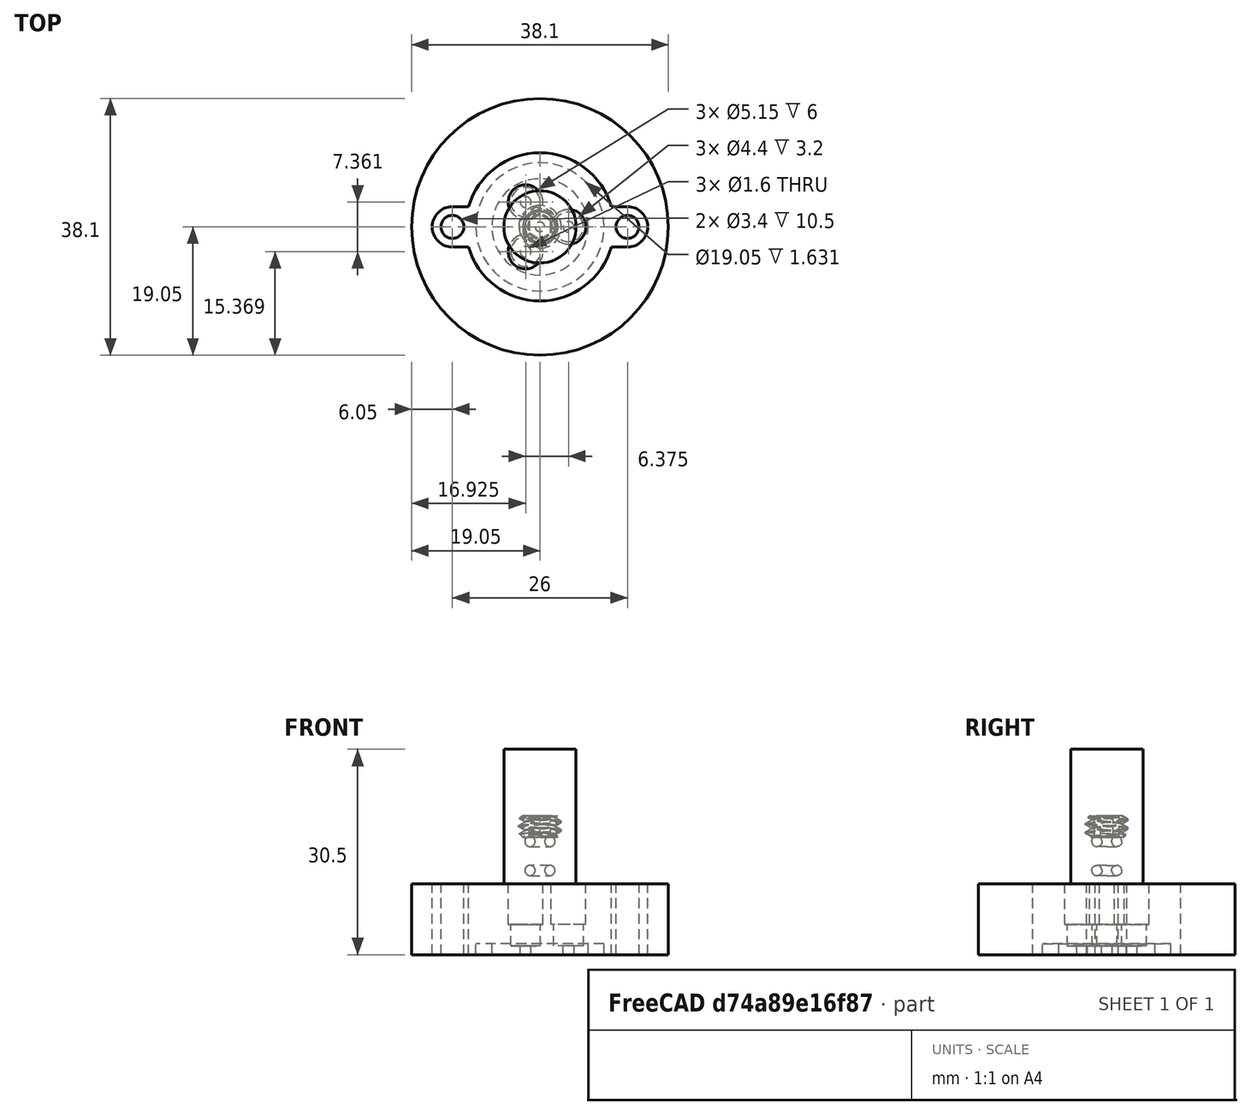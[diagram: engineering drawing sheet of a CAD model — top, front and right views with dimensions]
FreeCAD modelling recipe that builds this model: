
FCSTD DOCUMENT  (FreeCAD 0.18RUnknown)
Label: new_wire_fts_bottom
License: All rights reserved
LicenseURL: http://en.wikipedia.org/wiki/All_rights_reserved
objects: Part::Cylinder×21, Part::MultiFuse×6, Part::Cut×4, Part::Box×4, Part::FeaturePython×4, Part::Feature×3, Path::FeaturePython×3, App::FeaturePython×1, App::DocumentObjectGroup×1, Path::FeatureCompoundPython×1
note: 43 computed .brp shape members not serialized (recipe doc carries the construction recipe); baked Part::Feature solids carry a one-line shape summary decoded from their .brp

FEATURE [Part::Cylinder] Cylinder151  label="WireFeedsMount002"
  Angle = 360
  AttacherType = Attacher::AttachEngine3D
  Height = 11
  Placement = pos=(13,0,0) rot=(0,0,1;0rad)
  Radius = 1.7
FEATURE [Part::Cylinder] Cylinder155  label="Cylinder009"
  Angle = 360
  AttacherType = Attacher::AttachEngine3D
  Height = 2.38125
  Radius = 9.525
  expr: Radius = 3 / 4 * 25.399999999999999 / 2
  expr: Height = 3 / 32 * 25.399999999999999
FEATURE [Part::Cylinder] Cylinder154  label="Cylinder008"
  Angle = 360
  AttacherType = Attacher::AttachEngine3D
  Height = 2.38125
  Radius = 7.14375
  expr: Radius = 9 / 16 * 25.399999999999999 / 2
  expr: Height = 3 / 32 * 25.399999999999999
FEATURE [Part::Feature] Part__Feature001  label="TopOring"
  Placement = pos=(0,0,6.3) rot=(0,0,1;0rad)
  shape: bbox 4.839 x 4.839 x 1.524 mm, 4 faces (baked)
FEATURE [Part::Feature] Part__Feature002  label="BottomOring"
  Placement = pos=(0,0,2) rot=(0,0,1;0rad)
  shape: bbox 4.839 x 4.839 x 1.524 mm, 4 faces (baked)
FEATURE [Part::Cylinder] Cylinder153  label="Body"
  Angle = 360
  AttacherType = Attacher::AttachEngine3D
  Height = 10.5
  Radius = 11
FEATURE [Part::Cut] Cut019  label="Oring"
  Base = -> Cylinder155
  Placement = pos=(0,0,-0.75) rot=(0,0,1;0rad)
  Tool = -> Cylinder154
FEATURE [Part::Feature] Part__Feature  label="SetScrew"
  Placement = pos=(0,0,8.5) rot=(0,0,1;0rad)
  shape: bbox 6.351 x 6.351 x 4.446 mm, 26 faces (baked)
FEATURE [Part::Cylinder] Cylinder150  label="WireFeedsMount1"
  Angle = 360
  AttacherType = Attacher::AttachEngine3D
  Height = 11
  Placement = pos=(-13,0,0) rot=(0,0,1;0rad)
  Radius = 1.7
FEATURE [Part::Cylinder] Cylinder147  label="ThreadedSection"
  Angle = 360
  AttacherType = Attacher::AttachEngine3D
  Height = 6
  Placement = pos=(0,0,4.5) rot=(0,0,1;0rad)
  Radius = 2.575
  expr: Radius = 5.1500000000000004 / 2
FEATURE [Part::Cylinder] Cylinder152  label="RFFeeds005"
  Angle = 360
  AttacherType = Attacher::AttachEngine3D
  Height = 20
  Radius = 5.35813
  expr: Placement.Base.x = 0
FEATURE [Part::Cylinder] Cylinder156  label="BottomWireOutlet"
  Angle = 360
  AttacherType = Attacher::AttachEngine3D
  Height = 5
  Placement = pos=(0,0,-2) rot=(0,0,1;0rad)
  Radius = 0.8
FEATURE [Part::Cylinder] Cylinder157  label="SealSubtraction"
  Angle = 360
  AttacherType = Attacher::AttachEngine3D
  Height = 9
  Placement = pos=(0,0,1.3) rot=(0,0,1;0rad)
  Radius = 2.2
FEATURE [Part::Cylinder] Cylinder  label="MountFlange1"
  Angle = 360
  AttacherType = Attacher::AttachEngine3D
  Height = 10.5
  Placement = pos=(-13,0,0) rot=(0,0,1;0rad)
  Radius = 3
FEATURE [Part::Box] Box  label="MountCube1"
  AttacherType = Attacher::AttachEngine3D
  Height = 10.5
  Length = 3
  Placement = pos=(-13,-3,0) rot=(0,0,1;0rad)
  Width = 6
FEATURE [Part::Box] Box001  label="MountCube002"
  AttacherType = Attacher::AttachEngine3D
  Height = 10.5
  Length = 3
  Placement = pos=(10,-3,0) rot=(0,0,1;0rad)
  Width = 6
FEATURE [Part::Cylinder] Cylinder158  label="MountFlange002"
  Angle = 360
  AttacherType = Attacher::AttachEngine3D
  Height = 10.5
  Placement = pos=(13,0,0) rot=(0,0,1;0rad)
  Radius = 3
FEATURE [Part::MultiFuse] Fusion001
  Shapes = -> [Cylinder158,Box001,Box,Cylinder,Cylinder153]
FEATURE [Part::MultiFuse] Fusion
  Placement = pos=(4.25,0,0) rot=(0,0,1;0rad)
  Shapes = -> [Cylinder147,Cylinder157,Cylinder156]
FEATURE [Part::FeaturePython] Array  label="SealArray"  # Draft array (typed FeaturePython)
  Angle = 360
  ArrayType = 1
  Axis = (0,0,1)
  Base = -> Fusion
  Center = (0,0,0)
  Fuse = false
  IntervalAxis = (0,0,0)
  IntervalX = (1,0,0)
  IntervalY = (0,1,0)
  IntervalZ = (0,0,0)
  NumberPolar = 3
  NumberX = 2
  NumberY = 2
  NumberZ = 1
FEATURE [Part::MultiFuse] Fusion002
  Shapes = -> [Cylinder151,Cylinder150,Cut019,Array]
FEATURE [Part::Cut] Cut
  Base = -> Fusion001
  Placement = pos=(0,0,0) rot=(1,0,0;3.14159rad)
  Tool = -> Fusion002
FEATURE [Part::Cylinder] Cylinder160  label="Cylinder010"
  Angle = 360
  AttacherType = Attacher::AttachEngine3D
  Height = 2.38125
  Radius = 9.525
  expr: Radius = 3 / 4 * 25.399999999999999 / 2
  expr: Height = 3 / 32 * 25.399999999999999
FEATURE [Part::Cylinder] Cylinder161  label="WireFeedsMount003"
  Angle = 360
  AttacherType = Attacher::AttachEngine3D
  Height = 11
  Placement = pos=(-13,0,0) rot=(0,0,1;0rad)
  Radius = 1.7
FEATURE [Part::Cylinder] Cylinder162  label="ThreadedSection001"
  Angle = 360
  AttacherType = Attacher::AttachEngine3D
  Height = 6
  Placement = pos=(0,0,4.5) rot=(0,0,1;0rad)
  Radius = 2.575
  expr: Radius = 5.1500000000000004 / 2
FEATURE [Part::Cylinder] Cylinder163  label="Cylinder011"
  Angle = 360
  AttacherType = Attacher::AttachEngine3D
  Height = 2.38125
  Radius = 7.14375
  expr: Radius = 9 / 16 * 25.399999999999999 / 2
  expr: Height = 3 / 32 * 25.399999999999999
FEATURE [Part::Cut] Cut022  label="Oring001"
  Base = -> Cylinder160
  Placement = pos=(0,0,-0.75) rot=(0,0,1;0rad)
  Tool = -> Cylinder163
FEATURE [Part::Cylinder] Cylinder164  label="Body001"
  Angle = 360
  AttacherType = Attacher::AttachEngine3D
  Height = 10.5
  Radius = 11
FEATURE [Part::Cylinder] Cylinder165  label="WireFeedsMount004"
  Angle = 360
  AttacherType = Attacher::AttachEngine3D
  Height = 11
  Placement = pos=(13,0,0) rot=(0,0,1;0rad)
  Radius = 1.7
FEATURE [Part::Cylinder] Cylinder166  label="BottomWireOutlet001"
  Angle = 360
  AttacherType = Attacher::AttachEngine3D
  Height = 5
  Placement = pos=(0,0,-2) rot=(0,0,1;0rad)
  Radius = 0.8
FEATURE [Part::Cylinder] Cylinder167  label="SealSubtraction001"
  Angle = 360
  AttacherType = Attacher::AttachEngine3D
  Height = 9
  Placement = pos=(0,0,1.3) rot=(0,0,1;0rad)
  Radius = 2.2
FEATURE [Part::Box] Box002  label="MountCube003"
  AttacherType = Attacher::AttachEngine3D
  Height = 10.5
  Length = 3
  Placement = pos=(10,-3,0) rot=(0,0,1;0rad)
  Width = 6
FEATURE [Part::Box] Box003  label="MountCube004"
  AttacherType = Attacher::AttachEngine3D
  Height = 10.5
  Length = 3
  Placement = pos=(-13,-3,0) rot=(0,0,1;0rad)
  Width = 6
FEATURE [Part::MultiFuse] Fusion004
  Placement = pos=(4.25,0,0) rot=(0,0,1;0rad)
  Shapes = -> [Cylinder162,Cylinder167,Cylinder166]
FEATURE [Part::Cylinder] Cylinder168  label="MountFlange003"
  Angle = 360
  AttacherType = Attacher::AttachEngine3D
  Height = 10.5
  Placement = pos=(-13,0,0) rot=(0,0,1;0rad)
  Radius = 3
FEATURE [Part::Cylinder] Cylinder169  label="MountFlange004"
  Angle = 360
  AttacherType = Attacher::AttachEngine3D
  Height = 10.5
  Placement = pos=(13,0,0) rot=(0,0,1;0rad)
  Radius = 3
FEATURE [Part::MultiFuse] Fusion003
  Shapes = -> [Cylinder169,Box002,Box003,Cylinder168,Cylinder164]
FEATURE [Part::FeaturePython] Array001  label="SealArray001"  # Draft array (typed FeaturePython)
  Angle = 360
  ArrayType = 1
  Axis = (0,0,1)
  Base = -> Fusion004
  Center = (0,0,0)
  Fuse = false
  IntervalAxis = (0,0,0)
  IntervalX = (1,0,0)
  IntervalY = (0,1,0)
  IntervalZ = (0,0,0)
  NumberPolar = 3
  NumberX = 2
  NumberY = 2
  NumberZ = 1
FEATURE [Part::MultiFuse] Fusion005
  Shapes = -> [Cylinder165,Cylinder161,Cut022,Array001]
FEATURE [Part::Cut] Cut021
  Base = -> Fusion003
  Placement = pos=(0,0,-10.5) rot=(0,0,1;0rad)
  Tool = -> Fusion005
FEATURE [App::FeaturePython] SetupSheet  # Path/CAM operation (typed FeaturePython)
  ClearanceHeightExpression = StartDepth+SetupSheet.ClearanceHeightOffset
  ClearanceHeightOffset = 5
  FinalDepthExpression = OpFinalDepth
  HorizRapid = 0
  SafeHeightExpression = StartDepth+SetupSheet.SafeHeightOffset
  SafeHeightOffset = 3
  StartDepthExpression = OpStartDepth
  StepDownExpression = OpToolDiameter
  VertRapid = 0
FEATURE [Part::FeaturePython] Clone  label="Base-Cut"  # Draft clone (typed FeaturePython)
  AttacherType = Attacher::AttachEngine3D
  Fuse = false
  Objects = -> [Cut]
  PathResource = Base
  Placement = pos=(0,0,0) rot=(1,0,0;3.14159rad)
  Scale = (1,1,1)
FEATURE [Part::FeaturePython] Stock001  # WARN: FeaturePython — macro-defined, semantics opaque (R4)
  Height = 10.5
  Placement = pos=(0,0,-10.5) rot=(0,0,1;0rad)
  Radius = 19.05
  StockType = CreateCylinder
FEATURE [Path::FeaturePython] T3__063_End_Mill  label="T1: 063 End Mill"  # Path/CAM operation (typed FeaturePython)
  HorizFeed = 4
  HorizRapid = 0
  SpindleDir = 0
  SpindleSpeed = 24000
  ToolNumber = 1
  VertFeed = 0.6
  VertRapid = 0
  expr: HorizRapid = SetupSheet.HorizRapid
  expr: VertRapid = SetupSheet.VertRapid
FEATURE [Path::FeaturePython] Pocket_Shape  # Path/CAM operation (typed FeaturePython)
  Active = true
  AreaParams:
    OpenMode = 0
    Angle = 45.0
    MinArcPoints = 4
    Coplanar = 0
    Tolerance = 0.01
    CleanDistance = 0.0
    PocketExtraOffset = 0.0
    RoundPrecision = 0.0
    AngleShift = 0.0
    SubjectFill = 0
    PocketMode = 3
    PocketLastStepover = 0.0
    Simplify = False
    SectionTolerance = 1e-06
    MaxArcPoints = 100
    Offset = 0.0
    Accuracy = 0.01
    LastStepover = 0.0
    PocketStepover = 1.58
    ClipFill = 0
    ToolRadius = 0.79
    Outline = False
    ClipperScale = 10000000.0
    FromCenter = True
    Explode = False
    EndType = 0
    Shift = 0.0
    ExtraPass = 0
    Project = False
    JoinType = 0
    Thicken = False
    Stepdown = 1.0
    SectionMode = 2
    MiterLimit = 2.0
    Deflection = 0.01
    Reorient = True
    FitArcs = True
    SectionCount = -1
    SectionOffset = 0.0
    Stepover = 0.0
    Unit = 1.0
    Fill = 0
  Base = -> [Clone]
  ClearanceHeight = 5
  CutMode = 0
  ExtraOffset = 0
  FinalDepth = -1.63125
  FinishDepth = 0
  KeepToolDown = false
  MinTravel = false
  OffsetPattern = 2
  OpFinalDepth = -1.63125
  OpStartDepth = 0
  OpStockZMax = 0
  OpStockZMin = -10.5
  OpToolDiameter = 1.58
  PathParams = {'resume_height': 3.0, 'feedrate': 4.0, 'verbose': True, 'orientation': 1, 'return_end': True, 'preamble': False, 'retraction': 5.0, 'feedrate_v': 0.6}
  SafeHeight = 3
  StartAt = 0
  StartDepth = 0
  StartPoint = (0,0,0)
  StepDown = 0.5
  StepOver = 100
  ToolController = -> T3__063_End_Mill
  UseOutline = false
  UseStartPoint = false
  ZigZagAngle = 45
  expr: ClearanceHeight = StartDepth + SetupSheet.ClearanceHeightOffset
  expr: SafeHeight = StartDepth + SetupSheet.SafeHeightOffset
  expr: StepDown = 0.5
  expr: FinalDepth = OpFinalDepth
  expr: StartDepth = OpStartDepth
FEATURE [App::DocumentObjectGroup] Model
  Group = -> [Clone]
FEATURE [Path::FeatureCompoundPython] Operations001  label="Operations"  # Path/CAM operation (typed FeaturePython)
  Group = -> [Pocket_Shape]
  UsePlacements = false
FEATURE [Path::FeaturePython] Job  # Path/CAM operation (typed FeaturePython)
  GeometryTolerance = 0.01
  Model = -> Model
  Operations = -> Operations001
  PostProcessor = 6
  PostProcessorOutputFile = <userpath>/NAS/primary_a/Projects/ion_printer/files/ionprinter/mechanical/feedthroughs/new_wire_fts_gcode/bottom_ft_063_roughing.ngc
  SetupSheet = -> SetupSheet
  Stock = -> Stock001
  ToolController = -> [T3__063_End_Mill]
